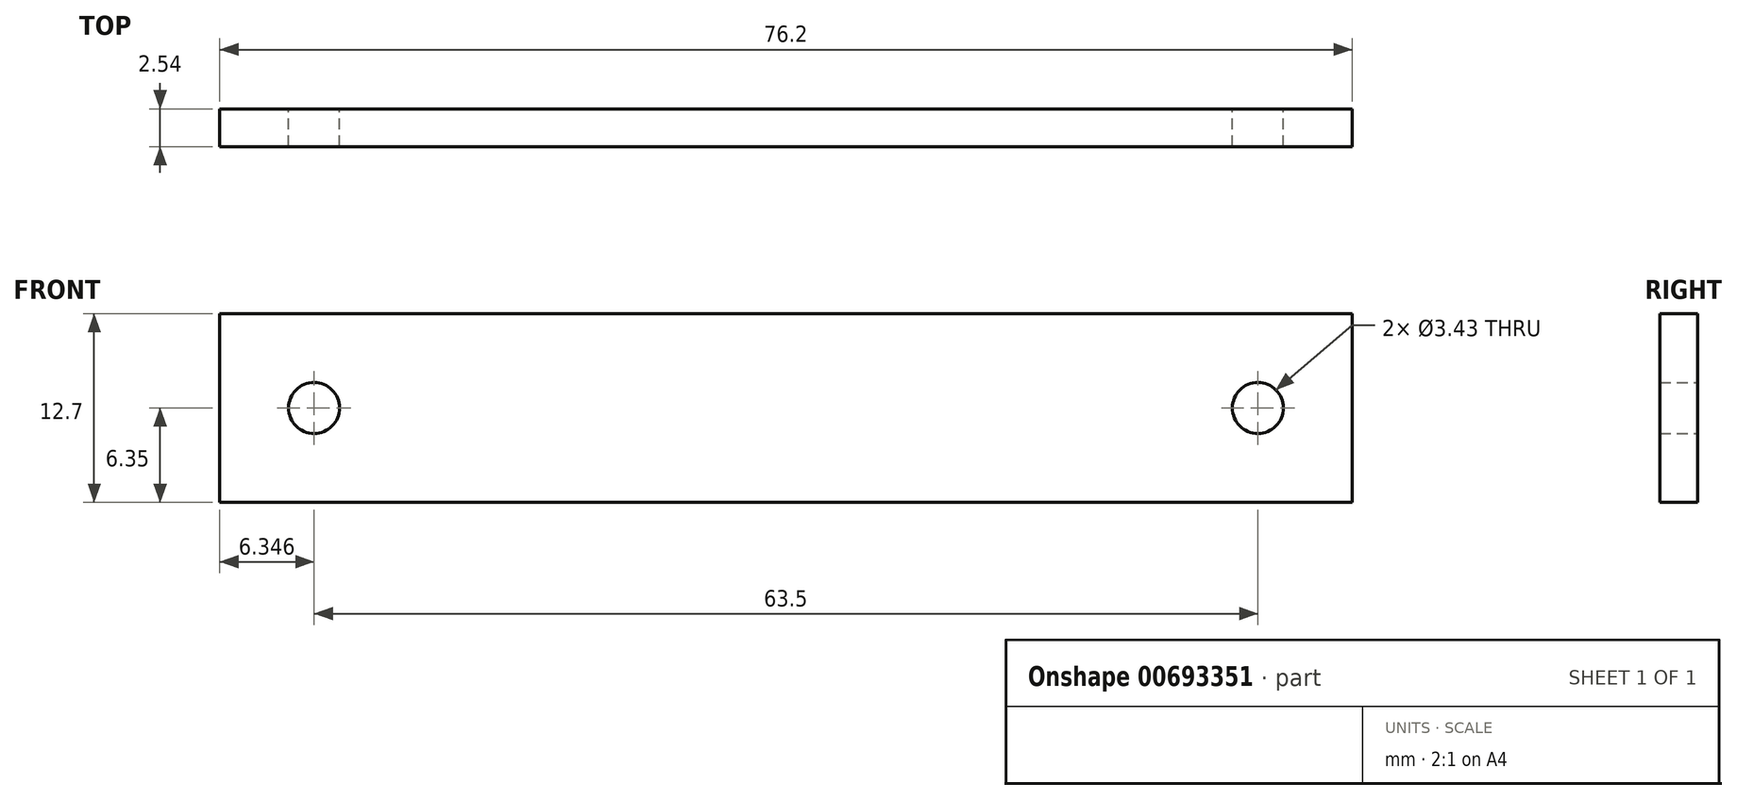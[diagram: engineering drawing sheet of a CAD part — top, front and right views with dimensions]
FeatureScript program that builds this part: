
annotation { "Feature Type Name" : "Feature", "Feature Type Description" : "" }
export const myFeature = defineFeature(function(context is Context, id is Id, definition is map)
    precondition{}
    {
        {
            var Q0;
            Q0=qCreatedBy(makeId("Front.planeOp"),FACE);
            var sketch = newSketch(context, id + "F0", { "sketchPlane" : qUnion([Q0])});
            skLineSegment(sketch, "E0.bottom", {"start": v(-34.75, 29.56) * mm, "end": v(41.45, 29.56) * mm});
            skLineSegment(sketch, "E0.top", {"start": v(-34.75, 16.86) * mm, "end": v(41.45, 16.86) * mm});
            skLineSegment(sketch, "E0.left", {"start": v(-34.75, 29.56) * mm, "end": v(-34.75, 16.86) * mm});
            skLineSegment(sketch, "E0.right", {"start": v(41.45, 29.56) * mm, "end": v(41.45, 16.86) * mm});
            skCircle(sketch, "E1", {"center": v(-28.4, 23.2) * mm, "radius": 1.71 * mm});
            skCircle(sketch, "E2", {"center": v(35.1, 23.2) * mm, "radius": 1.71 * mm});
            skPoint(sketch, "E2.centerSnap0", {"position": v(41.45, 23.2) * mm});
            skSolve(sketch);
        }
        {
            var Q0;
            Q0=makeQuery(id+"F0.imprint","IMPRINT",FACE,{"disambiguationData":[TD([[makeQuery(id+"F0.imprint","IMPRINT",EDGE,{"derivedFrom":sQuery(id+"F0.wireOp",EDGE,"E0.bottom")}),-1.0]])]});
            extrude(context, id + "F1", {"entities" : qUnion([Q0]), "endBound" : BoundingType.SYMMETRIC, "depth" : 2.54 * mm, "offsetDistance" : 25.4 * mm});
        }
    });
